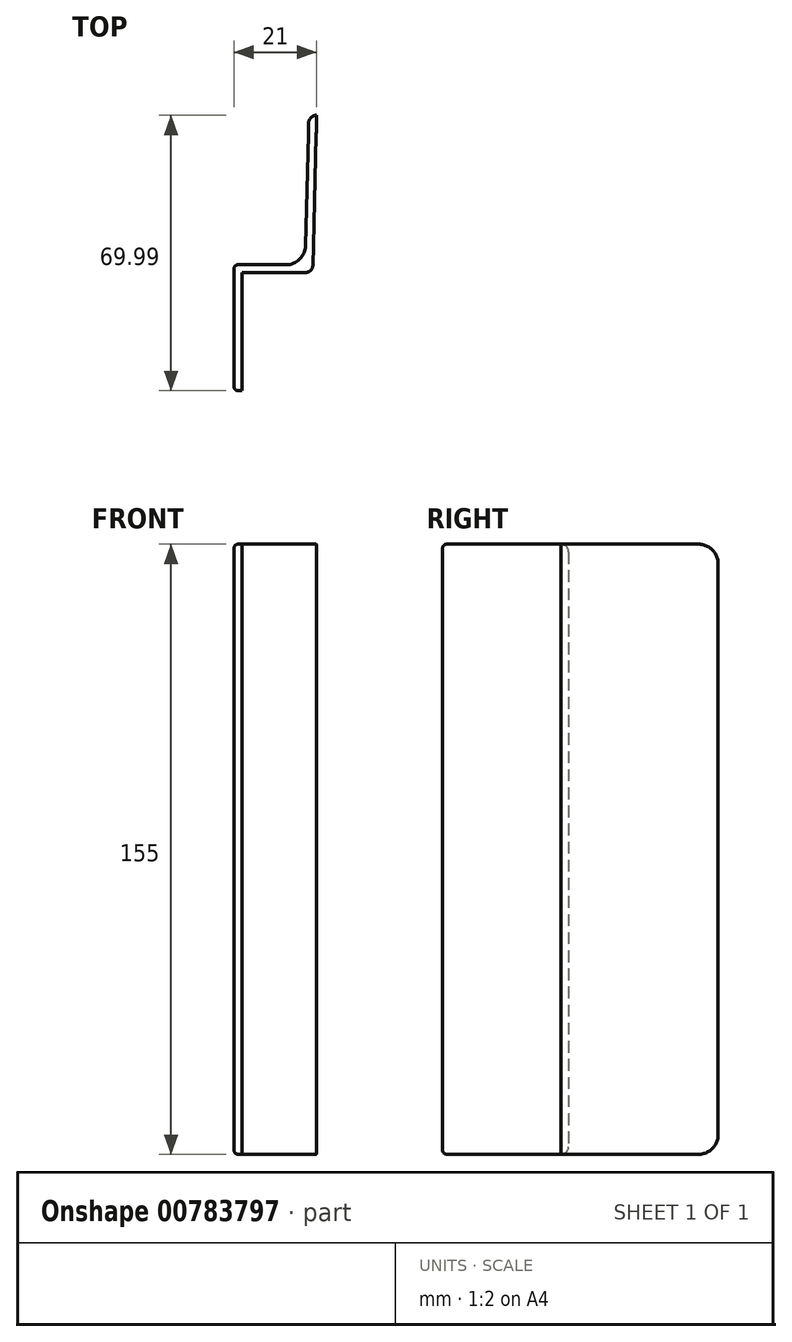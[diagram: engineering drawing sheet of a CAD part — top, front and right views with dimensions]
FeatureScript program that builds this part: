
annotation { "Feature Type Name" : "Feature", "Feature Type Description" : "" }
export const myFeature = defineFeature(function(context is Context, id is Id, definition is map)
    precondition{}
    {
        {
            var Q0;
            Q0=qCreatedBy(makeId("Top.planeOp"),FACE);
            var sketch = newSketch(context, id + "F0", { "sketchPlane" : qUnion([Q0])});
            skLineSegment(sketch, "E0", {"start": v(0, 0) * mm, "end": v(0, 30) * mm});
            skLineSegment(sketch, "E1", {"start": v(0, 30) * mm, "end": v(18, 30) * mm});
            skLineSegment(sketch, "E2.1", {"start": v(-2, 32) * mm, "end": v(16.05, 32) * mm});
            skLineSegment(sketch, "E2.2", {"start": v(-2, 0) * mm, "end": v(-2, 32) * mm});
            skLineSegment(sketch, "E3", {"start": v(19, 72.95) * mm, "end": v(19, 47.37) * mm, "construction": true});
            skLineSegment(sketch, "E4", {"start": v(18, 30) * mm, "end": v(19, 69.99) * mm});
            skLineSegment(sketch, "E5.0", {"start": v(16.05, 32) * mm, "end": v(17, 70.04) * mm});
            skLineSegment(sketch, "E6", {"start": v(17, 70.04) * mm, "end": v(19, 69.99) * mm});
            skLineSegment(sketch, "E7", {"start": v(-2, 0) * mm, "end": v(0, 0) * mm});
            skSolve(sketch);
        }
        {
            var Q0;
            Q0 = qSketchRegion(id + "F0", true);
            extrude(context, id + "F1", {"entities" : qUnion([Q0]), "depth" : 155 * mm, "offsetDistance" : 25 * mm});
        }
        {
            var Q0;
            Q0=makeQuery(id+"F1.opExtrude","SWEPT_EDGE",EDGE,{"disambiguationData":[OSD([sQuery(id+"F0.wireOp",EDGE,"E2.1"),sQuery(id+"F0.wireOp",EDGE,"E5.0")])]});
            var Q1;
            Q1=makeQuery(id+"F1.opExtrude","CAP_EDGE",EDGE,{"disambiguationData":[OSD([sQuery(id+"F0.wireOp",EDGE,"E6")])],"isStart":false});
            var Q2;
            Q2=makeQuery(id+"F1.opExtrude","CAP_EDGE",EDGE,{"disambiguationData":[OSD([sQuery(id+"F0.wireOp",EDGE,"E6")])],"isStart":true});
            fillet(context, id + "F2", {"entities" : qUnion([Q0, Q1, Q2]), "radius" : 5 * mm, "tangentPropagation" : true, "allowEdgeOverflow" : false});
        }
        {
            var Q0;
            Q0=makeQuery(id+"F1.opExtrude","SWEPT_FACE",FACE,{"disambiguationData":[OSD([sQuery(id+"F0.wireOp",EDGE,"E5.0")])]});
            fillet(context, id + "F3", {"entities" : qUnion([Q0]), "radius" : 2 * mm, "tangentPropagation" : true, "allowEdgeOverflow" : false});
        }
        {
            var Q0;
            Q0=makeQuery(id+"F1.opExtrude","SWEPT_EDGE",EDGE,{"disambiguationData":[OSD([sQuery(id+"F0.wireOp",EDGE,"E1"),sQuery(id+"F0.wireOp",EDGE,"E4")])]});
            fillet(context, id + "F4", {"entities" : qUnion([Q0]), "radius" : 2 * mm, "tangentPropagation" : true, "allowEdgeOverflow" : false});
        }
        {
            var Q0;
            Q0=makeQuery(id+"F1.opExtrude","SWEPT_EDGE",EDGE,{"disambiguationData":[OSD([sQuery(id+"F0.wireOp",EDGE,"E2.2"),sQuery(id+"F0.wireOp",EDGE,"E7")])]});
            fillet(context, id + "F5", {"entities" : qUnion([Q0]), "radius" : 1 * mm, "tangentPropagation" : true, "allowEdgeOverflow" : false});
        }
        {
            var Q0;
            Q0=makeQuery(id+"F1.opExtrude","SWEPT_EDGE",EDGE,{"disambiguationData":[OSD([sQuery(id+"F0.wireOp",EDGE,"E2.1"),sQuery(id+"F0.wireOp",EDGE,"E2.2")])]});
            fillet(context, id + "F6", {"entities" : qUnion([Q0]), "radius" : 1 * mm, "tangentPropagation" : true, "allowEdgeOverflow" : false});
        }
    });
